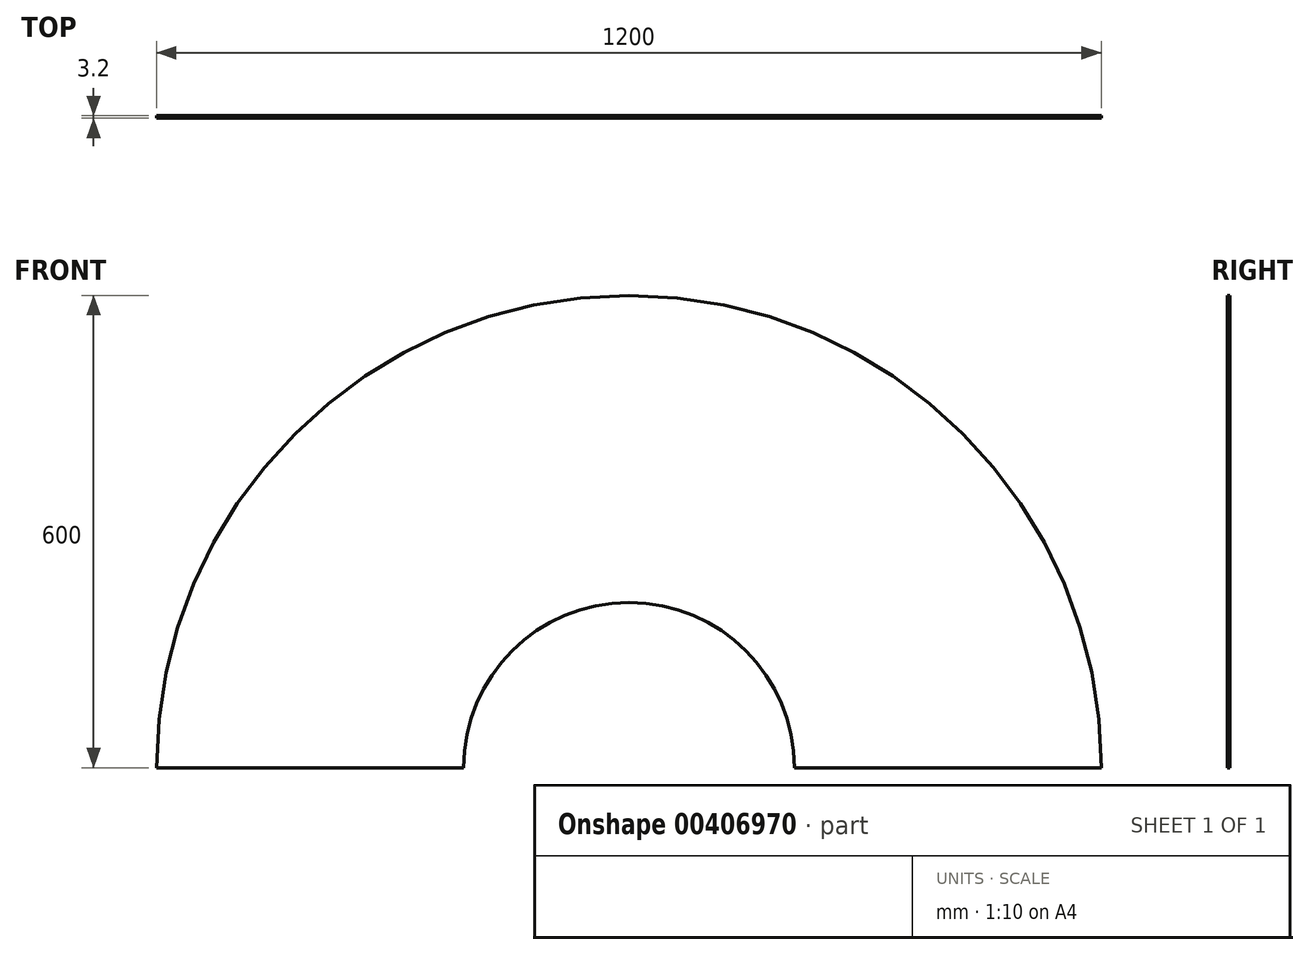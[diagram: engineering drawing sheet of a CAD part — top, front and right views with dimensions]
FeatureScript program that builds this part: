
annotation { "Feature Type Name" : "Feature", "Feature Type Description" : "" }
export const myFeature = defineFeature(function(context is Context, id is Id, definition is map)
    precondition{}
    {
        {
            var Q0;
            Q0=qCreatedBy(makeId("Front.planeOp"),FACE);
            var sketch = newSketch(context, id + "F0", { "sketchPlane" : qUnion([Q0])});
            skArc(sketch, "E0", {"start": v(600, 0) * mm, "mid": v(0, 600) * mm, "end": v(-600, 0) * mm});
            skLineSegment(sketch, "E1", {"start": v(-600, 0) * mm, "end": v(-210, 0) * mm});
            skArc(sketch, "E2", {"start": v(210, 0) * mm, "mid": v(0, 210) * mm, "end": v(-210, 0) * mm});
            skLineSegment(sketch, "E3.trimOffspring", {"start": v(210, 0) * mm, "end": v(600, 0) * mm});
            skSolve(sketch);
        }
        {
            var Q0;
            Q0=makeQuery(id+"F0.imprint","IMPRINT",FACE,{"disambiguationData":[TD([[makeQuery(id+"F0.imprint","IMPRINT",EDGE,{"derivedFrom":sQuery(id+"F0.wireOp",EDGE,"E0")}),1.0]])]});
            extrude(context, id + "F1", {"entities" : qUnion([Q0]), "depth" : 3.2 * mm});
        }
    });
